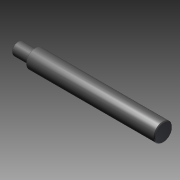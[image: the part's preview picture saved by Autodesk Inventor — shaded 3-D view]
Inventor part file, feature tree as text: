
AUTODESK INVENTOR PART (.ipt)
format: ipt  version: 2016 (Build 200138000, 138)  size: 103,424 bytes
history: native  units: mm
features: revolve x1, sketch x1
ambient origin geometry x8: Origin, YZ Plane, XZ Plane, XY Plane, X Axis, Y Axis, Z Axis, Center Point
bodies: Solid1 (feature_tree)
feature tree (2):
  revolve  "Revolution1"  [1 undecoded]
  sketch  "Sketch_1"  dims[d0=360.0deg]
note: 1 required parameter value undecoded (feature->parameter linkage not recoverable at this tier; creation-order binding heuristic only, values carry confidence <= 0.55)
